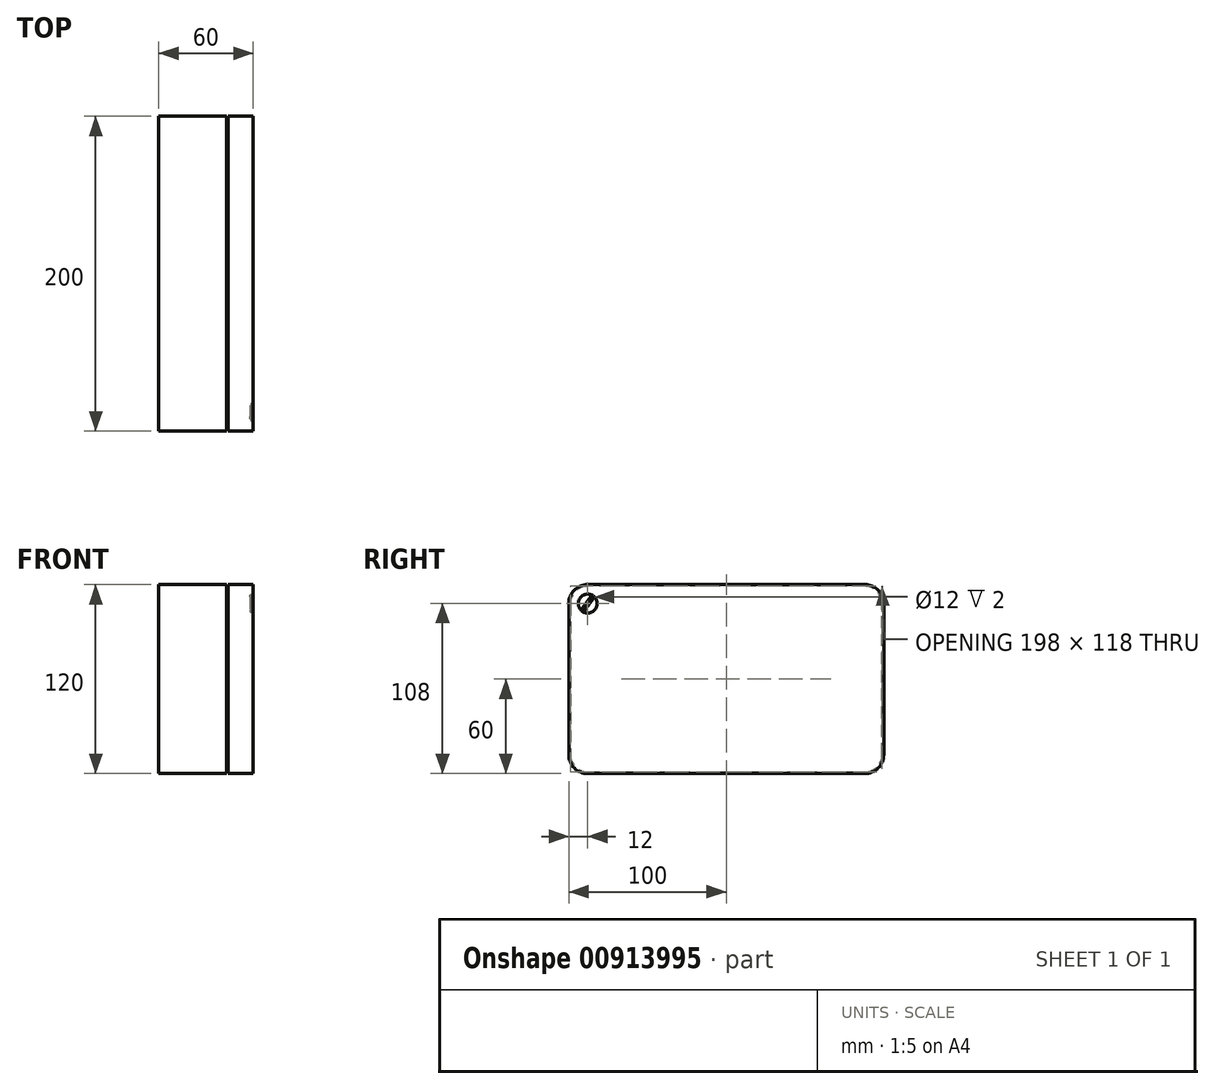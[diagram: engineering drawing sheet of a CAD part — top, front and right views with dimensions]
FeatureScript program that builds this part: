
annotation { "Feature Type Name" : "Feature", "Feature Type Description" : "" }
export const myFeature = defineFeature(function(context is Context, id is Id, definition is map)
    precondition{}
    {
        {
            var Q0;
            Q0=qCreatedBy(makeId("Right.planeOp"),FACE);
            var sketch = newSketch(context, id + "F0", { "sketchPlane" : qUnion([Q0])});
            skLineSegment(sketch, "E0.bottom", {"start": v(-100, 60) * mm, "end": v(100, 60) * mm});
            skLineSegment(sketch, "E0.top", {"start": v(-100, -60) * mm, "end": v(100, -60) * mm});
            skLineSegment(sketch, "E0.left", {"start": v(-100, 60) * mm, "end": v(-100, -60) * mm});
            skLineSegment(sketch, "E0.right", {"start": v(100, 60) * mm, "end": v(100, -60) * mm});
            skLineSegment(sketch, "E1", {"start": v(-100, 60) * mm, "end": v(100, -60) * mm, "construction": true});
            skSolve(sketch);
        }
        {
            var Q0;
            Q0 = qSketchRegion(id + "F0", true);
            extrude(context, id + "F1", {"entities" : qUnion([Q0]), "oppositeDirection" : true, "depth" : 60 * mm, "offsetDistance" : 25 * mm});
        }
        {
            var Q0;
            Q0=makeQuery(id+"F1.opExtrude","SWEPT_EDGE",EDGE,{"disambiguationData":[OSD([sQuery(id+"F0.wireOp",EDGE,"E0.bottom"),sQuery(id+"F0.wireOp",EDGE,"E0.left")])]});
            var Q1;
            Q1=makeQuery(id+"F1.opExtrude","SWEPT_EDGE",EDGE,{"disambiguationData":[OSD([sQuery(id+"F0.wireOp",EDGE,"E0.top"),sQuery(id+"F0.wireOp",EDGE,"E0.left")])]});
            var Q2;
            Q2=makeQuery(id+"F1.opExtrude","SWEPT_EDGE",EDGE,{"disambiguationData":[OSD([sQuery(id+"F0.wireOp",EDGE,"E0.top"),sQuery(id+"F0.wireOp",EDGE,"E0.right")])]});
            var Q3;
            Q3=makeQuery(id+"F1.opExtrude","SWEPT_EDGE",EDGE,{"disambiguationData":[OSD([sQuery(id+"F0.wireOp",EDGE,"E0.bottom"),sQuery(id+"F0.wireOp",EDGE,"E0.right")])]});
            fillet(context, id + "F2", {"entities" : qUnion([Q0, Q1, Q2, Q3]), "radius" : 12 * mm, "tangentPropagation" : true, "allowEdgeOverflow" : false});
        }
        {
            var Q0;
            Q0=makeQuery(id+"F1.opExtrude","CAP_FACE",FACE,{"disambiguationData":[OSD([sQuery(id+"F0.wireOp",EDGE,"E0.bottom"),sQuery(id+"F0.wireOp",EDGE,"E0.top"),sQuery(id+"F0.wireOp",EDGE,"E0.left"),sQuery(id+"F0.wireOp",EDGE,"E0.right")])],"isStart":true});
            cPlane(context, id + "F3", {"entities" : qUnion([Q0]), "cplaneType" : CPlaneType.OFFSET, "offset" : 16 * mm, "oppositeDirection" : true, "width" : 150 * mm, "height" : 150 * mm});
        }
        {
            var Q0;
            Q0=qCreatedBy(id+"F3.planeOp",FACE);
            var sketch = newSketch(context, id + "F4", { "sketchPlane" : qUnion([Q0])});
            skArc(sketch, "E2.0", {"start": v(-88, 59) * mm, "mid": v(-95.78, 55.78) * mm, "end": v(-99, 48) * mm});
            skLineSegment(sketch, "E2.1", {"start": v(88, 59) * mm, "end": v(-88, 59) * mm});
            skLineSegment(sketch, "E2.2", {"start": v(-99, 48) * mm, "end": v(-99, -48) * mm});
            skArc(sketch, "E2.3", {"start": v(99, 48) * mm, "mid": v(95.78, 55.78) * mm, "end": v(88, 59) * mm});
            skArc(sketch, "E2.4", {"start": v(-99, -48) * mm, "mid": v(-95.78, -55.78) * mm, "end": v(-88, -59) * mm});
            skLineSegment(sketch, "E2.5", {"start": v(-88, -59) * mm, "end": v(88, -59) * mm});
            skArc(sketch, "E2.6", {"start": v(88, -59) * mm, "mid": v(95.78, -55.78) * mm, "end": v(99, -48) * mm});
            skLineSegment(sketch, "E2.7", {"start": v(99, -48) * mm, "end": v(99, 48) * mm});
            skLineSegment(sketch, "E3.0.0", {"start": v(-100, 48) * mm, "end": v(-100, -48) * mm});
            skArc(sketch, "E3.0.1", {"start": v(-100, -48) * mm, "mid": v(-96.49, -56.49) * mm, "end": v(-88, -60) * mm});
            skLineSegment(sketch, "E3.0.2", {"start": v(-88, -60) * mm, "end": v(88, -60) * mm});
            skArc(sketch, "E3.0.3", {"start": v(88, -60) * mm, "mid": v(96.49, -56.49) * mm, "end": v(100, -48) * mm});
            skLineSegment(sketch, "E3.0.4", {"start": v(100, -48) * mm, "end": v(100, 48) * mm});
            skArc(sketch, "E3.0.5", {"start": v(100, 48) * mm, "mid": v(96.49, 56.49) * mm, "end": v(88, 60) * mm});
            skLineSegment(sketch, "E3.0.6", {"start": v(88, 60) * mm, "end": v(-88, 60) * mm});
            skArc(sketch, "E3.0.7", {"start": v(-88, 60) * mm, "mid": v(-96.49, 56.49) * mm, "end": v(-100, 48) * mm});
            skSolve(sketch);
        }
        {
            var Q0;
            Q0 = qSketchRegion(id + "F4", true);
            extrude(context, id + "F5", {"entities" : qUnion([Q0]), "operationType" : NewBodyOperationType.REMOVE, "oppositeDirection" : true, "depth" : 1 * mm, "offsetDistance" : 25 * mm});
        }
        {
            var Q0;
            Q0=makeQuery(id+"F1.opExtrude","CAP_FACE",FACE,{"disambiguationData":[OSD([sQuery(id+"F0.wireOp",EDGE,"E0.bottom"),sQuery(id+"F0.wireOp",EDGE,"E0.top"),sQuery(id+"F0.wireOp",EDGE,"E0.left"),sQuery(id+"F0.wireOp",EDGE,"E0.right")])],"isStart":true});
            var sketch = newSketch(context, id + "F6", { "sketchPlane" : qUnion([Q0])});
            skCircle(sketch, "E4", {"center": v(-88, 48) * mm, "radius": 6 * mm});
            skSolve(sketch);
        }
        {
            var Q0;
            Q0=makeQuery(id+"F6.imprint","IMPRINT",FACE,{"disambiguationData":[TD([[makeQuery(id+"F6.imprint","IMPRINT",EDGE,{"derivedFrom":sQuery(id+"F6.wireOp",EDGE,"E4")}),1.0]])]});
            extrude(context, id + "F7", {"entities" : qUnion([Q0]), "operationType" : NewBodyOperationType.REMOVE, "oppositeDirection" : true, "depth" : 1 * mm, "offsetDistance" : 25 * mm});
        }
        {
            var Q0;
            Q0=makeQuery(id+"F7.boolean.opBoolean","COPY",FACE,{"derivedFrom":makeQuery(id+"F7.opExtrude","CAP_FACE",FACE,{"disambiguationData":[OSD([sQuery(id+"F6.wireOp",EDGE,"E4")])],"isStart":false})});
            var sketch = newSketch(context, id + "F8", { "sketchPlane" : qUnion([Q0])});
            skCircle(sketch, "E5.0", {"center": v(-88, 48) * mm, "radius": 6 * mm});
            skLineSegment(sketch, "E6", {"start": v(-85.19, 53.3) * mm, "end": v(-92.4, 43.92) * mm});
            skLineSegment(sketch, "E7", {"start": v(-83.6, 52.08) * mm, "end": v(-90.81, 42.7) * mm});
            skLineSegment(sketch, "E8", {"start": v(-90.81, 42.7) * mm, "end": v(-85.19, 53.3) * mm, "construction": true});
            skSolve(sketch);
        }
        {
            var Q0;
            {var subQ0=sQuery(id+"F8.wireOp",EDGE,"E6");Q0=makeQuery(id+"F8.imprint","IMPRINT",FACE,{"disambiguationData":[TD([[makeQuery(id+"F8.imprint","IMPRINT",EDGE,{"derivedFrom":subQ0}),1.0]])]});}
            extrude(context, id + "F9", {"entities" : qUnion([Q0]), "operationType" : NewBodyOperationType.REMOVE, "oppositeDirection" : true, "depth" : 1 * mm, "offsetDistance" : 25 * mm});
        }
    });
